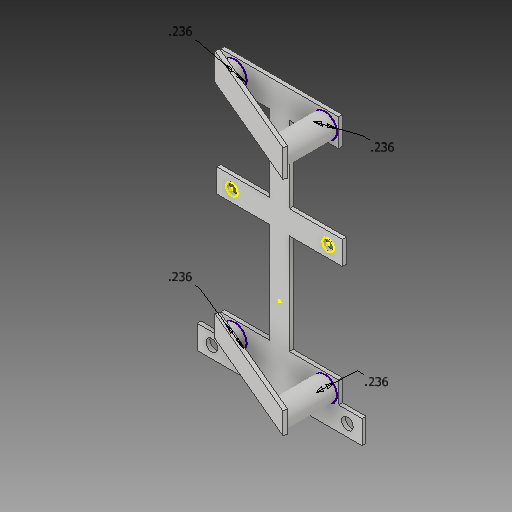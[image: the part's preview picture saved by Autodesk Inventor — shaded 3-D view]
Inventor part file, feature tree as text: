
AUTODESK INVENTOR PART (.ipt)
format: ipt  version: 2018 (Build 220112000, 112)  size: 247,296 bytes
history: native  units: in
note: dims shown in document units (in); Inventor stores cm internally (conversion verified against a paired STEP export)
features: extrude x9, sketch x7
ambient origin geometry x8: Origin, YZ Plane, XZ Plane, XY Plane, X Axis, Y Axis, Z Axis, Center Point
bodies: Solid1 (feature_tree)
feature tree (16):
  extrude  "Extrusion1"  Depth=1.2598in
  extrude  "Extrusion2"  TaperAngle=0.0deg  [1 undecoded]
  extrude  "Extrusion3"  Depth=0.2362in
  sketch  "Sketch5"  dims[d7=0.0in d8=0.0394in d9=0.0in]
  extrude  "Extrusion5"  Depth=0.0394in TaperAngle=0.0deg
  extrude  "Extrusion6"  Depth=0.6791in
  sketch  "Sketch8"  dims[d14=0.6791in d15=0.1181in]
  extrude  "Extrusion9"  Depth=0.1181in
  extrude  "Extrusion10"  Depth=0.0394in
  extrude  "Extrusion11"  Depth=0.0394in
  extrude  "Extrusion12"  Depth=0.0394in
  sketch  "Sketch1"  dims[d0=0.1969in d2=1.2598in]
  sketch  "Sketch2"  dims[d3=0.2362in d4=0.0in]
  sketch  "Sketch4"  dims[d5=1.6535in d6=0.2362in]
  sketch  "Sketch6"  dims[d10=1.3583in d13=0.6791in]
  sketch  "Sketch9"  dims[d16=0.1181in d17=0.9646in d18=0.4823in d19=0.4823in d20=0.1181in d21=0.1181in d22=0.0787in d23=0.0in d28=2.2835in d29=0.1969in d30=0.0in d31=0.0in d32=0.1969in d33=1.1811in d34=1.1811in d35=0.2756in d36=0.2756in d37=0.0787in d38=0.0787in d39=0.0787in d40=0.0787in d41=0.9055in d42=0.9055in d43=0.4528in d44=0.4528in d45=0.4528in d46=0.4528in d47=0.0394in d48=0.0in d51=0.2362in d52=0.2362in d55=0.2362in d56=0.2362in d57=0.0787in d58=0.0in d59=0.2362in d60=0.2362in d61=0.2362in d62=0.2362in d63=0.0787in d64=0.0in d65=1.4567in d66=1.4567in d72=0.4604in d73=0.25in d74=0.0in d75=0.5in d76=0.0in d77=3.0in d78=0.0in d79=0.0394in d80=0.0in]
note: 1 required parameter value undecoded (feature->parameter linkage not recoverable at this tier; creation-order binding heuristic only, values carry confidence <= 0.55)
